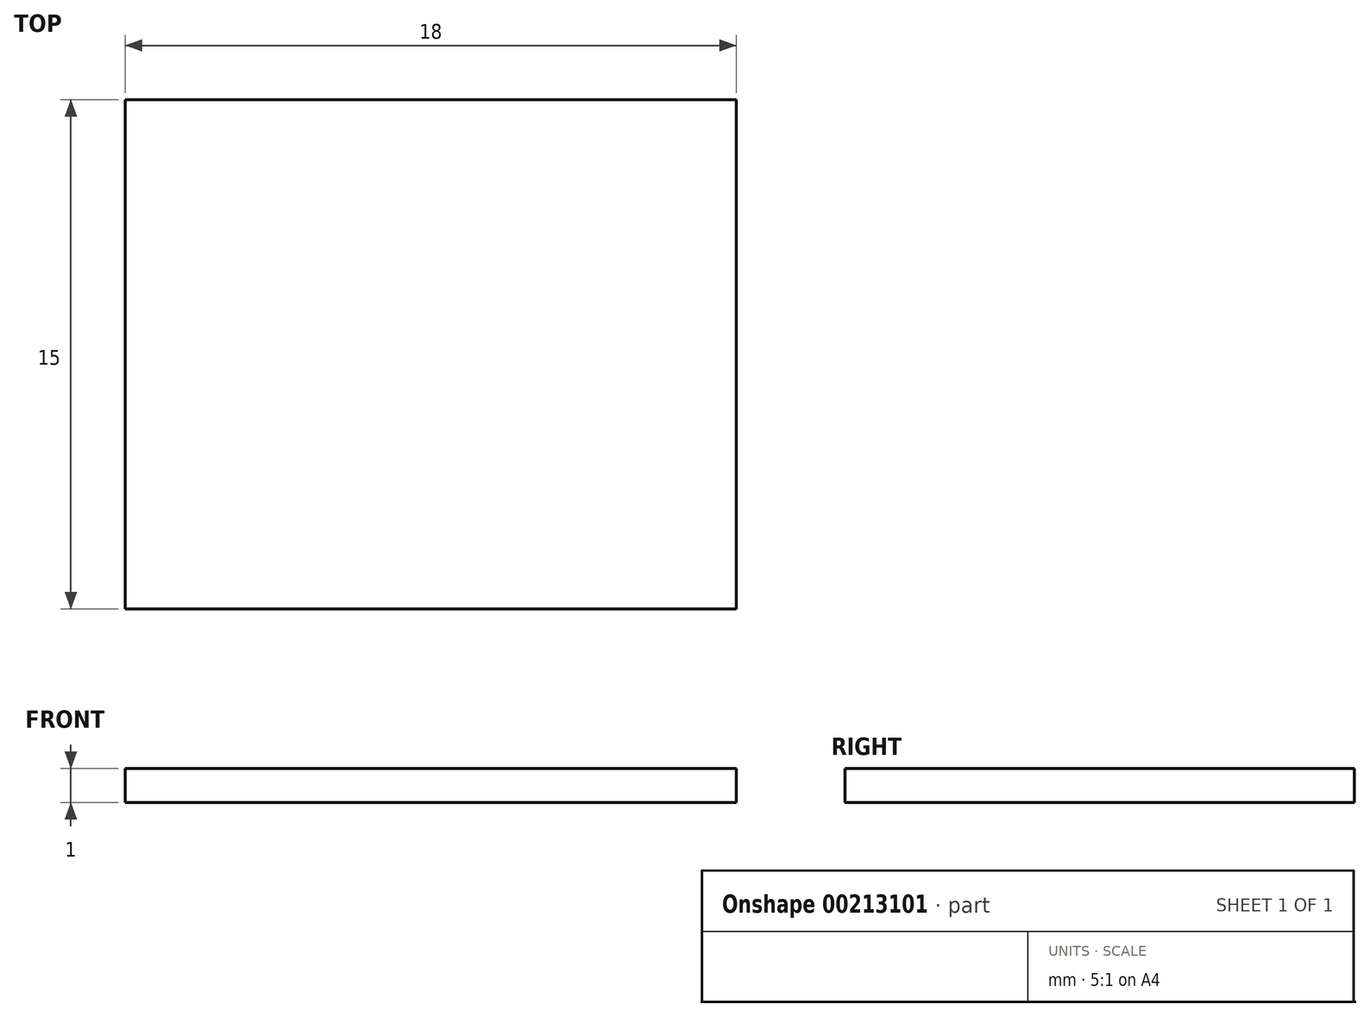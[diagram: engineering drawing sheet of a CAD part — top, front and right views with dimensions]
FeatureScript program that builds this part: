
annotation { "Feature Type Name" : "Feature", "Feature Type Description" : "" }
export const myFeature = defineFeature(function(context is Context, id is Id, definition is map)
    precondition{}
    {
        {
            var Q0;
            Q0=qCreatedBy(makeId("Top.planeOp"),FACE);
            var sketch = newSketch(context, id + "F0", { "sketchPlane" : qUnion([Q0])});
            skLineSegment(sketch, "E0.bottom", {"start": v(0, 0) * mm, "end": v(18, 0) * mm});
            skLineSegment(sketch, "E0.top", {"start": v(0, -15) * mm, "end": v(18, -15) * mm});
            skLineSegment(sketch, "E0.left", {"start": v(0, 0) * mm, "end": v(0, -15) * mm});
            skLineSegment(sketch, "E0.right", {"start": v(18, 0) * mm, "end": v(18, -15) * mm});
            skSolve(sketch);
        }
        {
            var Q0;
            Q0 = qSketchRegion(id + "F0", true);
            extrude(context, id + "F1", {"entities" : qUnion([Q0]), "depth" : 1 * mm});
        }
    });
